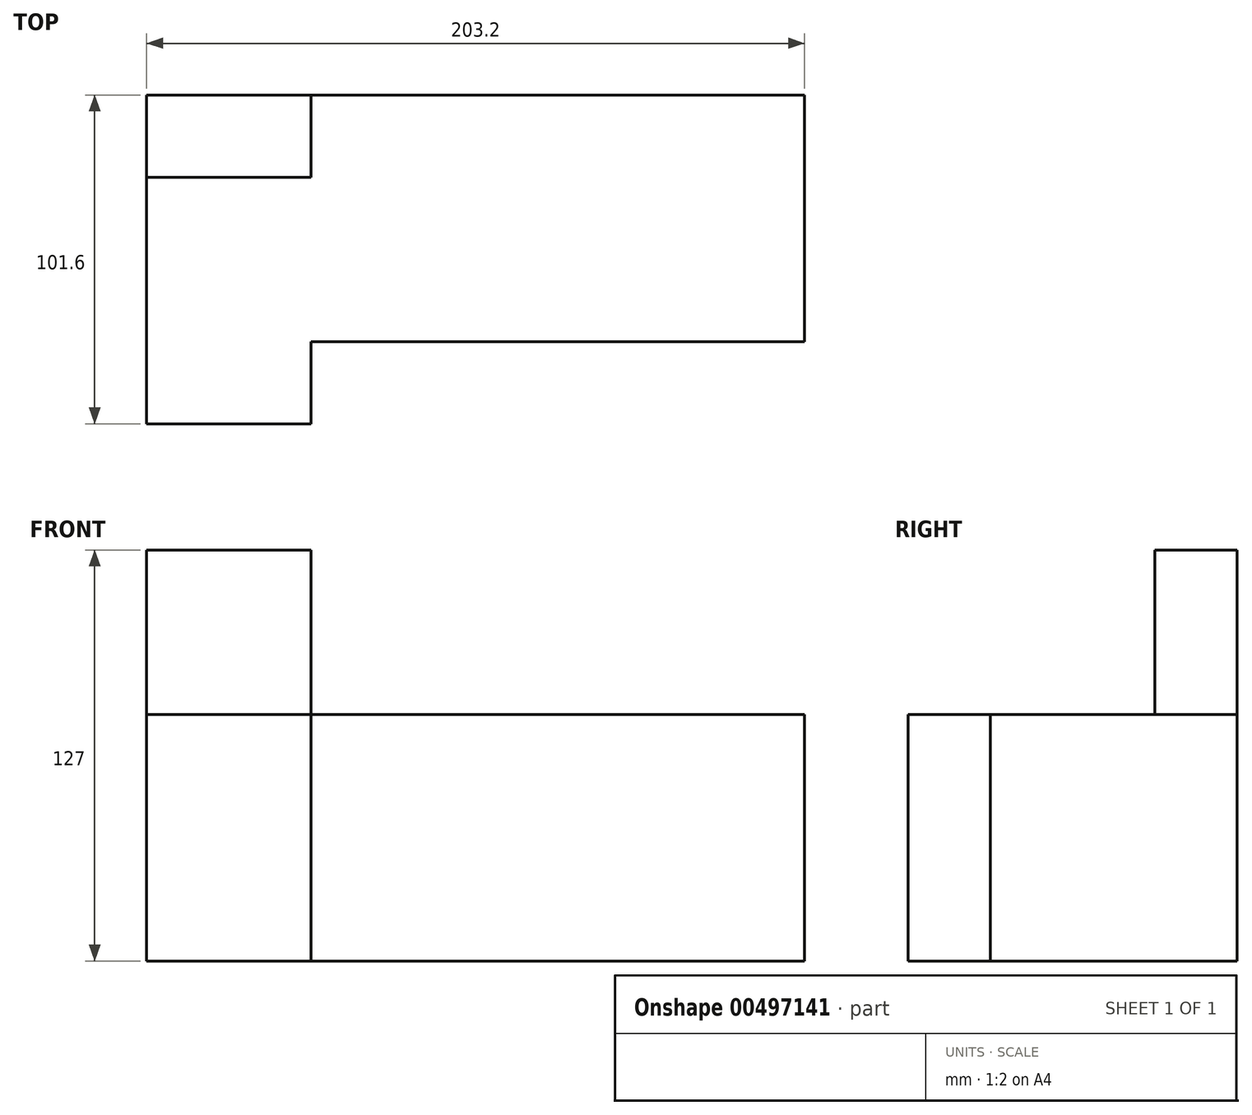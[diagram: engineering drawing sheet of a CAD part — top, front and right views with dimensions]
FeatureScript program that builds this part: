
annotation { "Feature Type Name" : "Feature", "Feature Type Description" : "" }
export const myFeature = defineFeature(function(context is Context, id is Id, definition is map)
    precondition{}
    {
        {
            var Q0;
            Q0=qCreatedBy(makeId("Front.planeOp"),FACE);
            var sketch = newSketch(context, id + "F0", { "sketchPlane" : qUnion([Q0])});
            skLineSegment(sketch, "E0.bottom", {"start": v(-101.84, 16.08) * mm, "end": v(101.36, 16.08) * mm});
            skLineSegment(sketch, "E0.top", {"start": v(-101.84, -60.12) * mm, "end": v(101.36, -60.12) * mm});
            skLineSegment(sketch, "E0.left", {"start": v(-101.84, 16.08) * mm, "end": v(-101.84, -60.12) * mm});
            skLineSegment(sketch, "E0.right", {"start": v(101.36, 16.08) * mm, "end": v(101.36, -60.12) * mm});
            skSolve(sketch);
        }
        {
            var Q0;
            Q0=makeQuery(id+"F0.imprint","IMPRINT",FACE,{"disambiguationData":[TD([[makeQuery(id+"F0.imprint","IMPRINT",EDGE,{"derivedFrom":sQuery(id+"F0.wireOp",EDGE,"E0.bottom")}),-1.0]])]});
            extrude(context, id + "F1", {"entities" : qUnion([Q0]), "depth" : 76.2 * mm});
        }
        {
            var Q0;
            Q0=makeQuery(id+"F1.opExtrude","CAP_FACE",FACE,{"disambiguationData":[OSD([sQuery(id+"F0.wireOp",EDGE,"E0.bottom"),sQuery(id+"F0.wireOp",EDGE,"E0.top"),sQuery(id+"F0.wireOp",EDGE,"E0.left"),sQuery(id+"F0.wireOp",EDGE,"E0.right")])],"isStart":false});
            var sketch = newSketch(context, id + "F2", { "sketchPlane" : qUnion([Q0])});
            skLineSegment(sketch, "E1.bottom", {"start": v(-101.84, -60.12) * mm, "end": v(-51.04, -60.12) * mm});
            skLineSegment(sketch, "E1.top", {"start": v(-101.84, 16.08) * mm, "end": v(-51.04, 16.08) * mm});
            skLineSegment(sketch, "E1.left", {"start": v(-101.84, -60.12) * mm, "end": v(-101.84, 16.08) * mm});
            skLineSegment(sketch, "E1.right", {"start": v(-51.04, -60.12) * mm, "end": v(-51.04, 16.08) * mm});
            skSolve(sketch);
        }
        {
            var Q0;
            Q0 = qSketchRegion(id + "F2", true);
            extrude(context, id + "F3", {"entities" : qUnion([Q0]), "operationType" : NewBodyOperationType.ADD, "depth" : 25.4 * mm});
        }
        {
            var Q0;
            Q0=makeQuery(id+"F3.boolean.opBoolean","MERGE",FACE,{"derivedFrom":[makeQuery(id+"F1.opExtrude","SWEPT_FACE",FACE,{"disambiguationData":[OSD([sQuery(id+"F0.wireOp",EDGE,"E0.bottom")])]}),makeQuery(id+"F3.opExtrude","SWEPT_FACE",FACE,{"disambiguationData":[OSD([sQuery(id+"F2.wireOp",EDGE,"E1.top")])]})]});
            var sketch = newSketch(context, id + "F4", { "sketchPlane" : qUnion([Q0])});
            skLineSegment(sketch, "E2.bottom", {"start": v(-101.84, 0) * mm, "end": v(-51.04, 0) * mm});
            skLineSegment(sketch, "E2.top", {"start": v(-101.84, -25.4) * mm, "end": v(-51.04, -25.4) * mm});
            skLineSegment(sketch, "E2.left", {"start": v(-101.84, 0) * mm, "end": v(-101.84, -25.4) * mm});
            skLineSegment(sketch, "E2.right", {"start": v(-51.04, 0) * mm, "end": v(-51.04, -25.4) * mm});
            skSolve(sketch);
        }
        {
            var Q0;
            Q0 = qSketchRegion(id + "F4", true);
            extrude(context, id + "F5", {"entities" : qUnion([Q0]), "operationType" : NewBodyOperationType.ADD, "depth" : 50.8 * mm});
        }
    });
